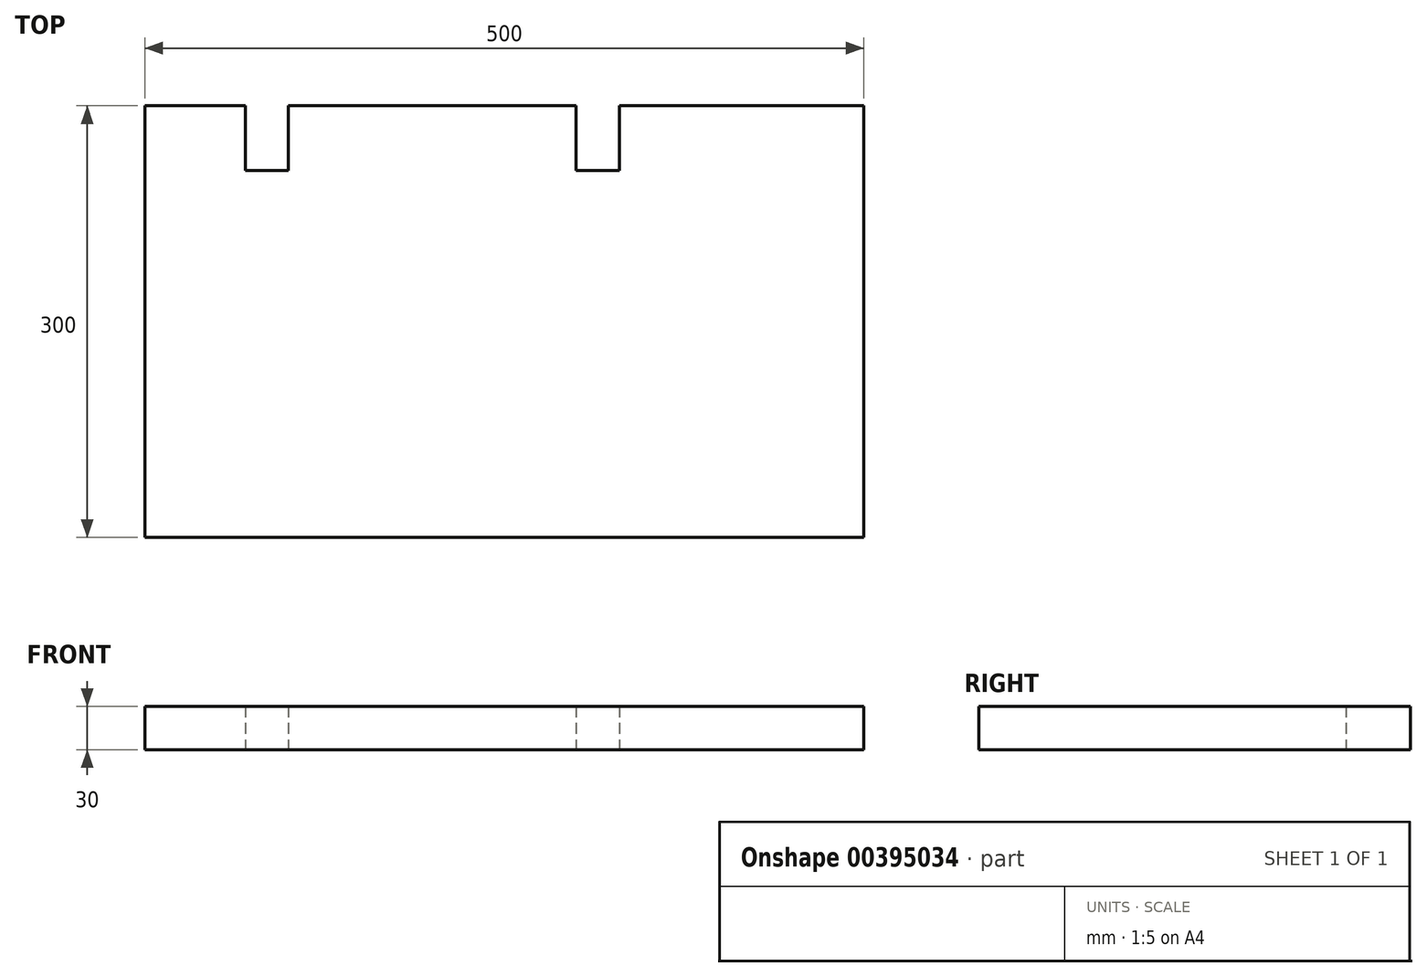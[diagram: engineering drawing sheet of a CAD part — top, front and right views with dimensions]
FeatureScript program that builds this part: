
annotation { "Feature Type Name" : "Feature", "Feature Type Description" : "" }
export const myFeature = defineFeature(function(context is Context, id is Id, definition is map)
    precondition{}
    {
        {
            var Q0;
            Q0=qCreatedBy(makeId("Front.planeOp"),FACE);
            var sketch = newSketch(context, id + "F0", { "sketchPlane" : qUnion([Q0])});
            skLineSegment(sketch, "E0.bottom", {"start": v(-250, 15) * mm, "end": v(250, 15) * mm});
            skLineSegment(sketch, "E0.top", {"start": v(-250, -15) * mm, "end": v(250, -15) * mm});
            skLineSegment(sketch, "E0.left", {"start": v(-250, 15) * mm, "end": v(-250, -15) * mm});
            skLineSegment(sketch, "E0.right", {"start": v(250, 15) * mm, "end": v(250, -15) * mm});
            skPoint(sketch, "E0.middle", {"position": v(0, 0) * mm});
            skSolve(sketch);
        }
        {
            var Q0;
            Q0=makeQuery(id+"F0.imprint","IMPRINT",FACE,{"disambiguationData":[TD([[makeQuery(id+"F0.imprint","IMPRINT",EDGE,{"derivedFrom":sQuery(id+"F0.wireOp",EDGE,"E0.bottom")}),-1.0]])]});
            extrude(context, id + "F1", {"entities" : qUnion([Q0]), "depth" : 300 * mm});
        }
        {
            var Q0;
            Q0=qCreatedBy(makeId("Front.planeOp"),FACE);
            var sketch = newSketch(context, id + "F2", { "sketchPlane" : qUnion([Q0])});
            skLineSegment(sketch, "E1.bottom", {"start": v(80, 15) * mm, "end": v(50, 15) * mm});
            skLineSegment(sketch, "E1.top", {"start": v(80, -15) * mm, "end": v(50, -15) * mm});
            skLineSegment(sketch, "E1.left", {"start": v(50, 15) * mm, "end": v(50, -15) * mm});
            skLineSegment(sketch, "E1.right", {"start": v(80, 15) * mm, "end": v(80, -15) * mm});
            skSolve(sketch);
        }
        {
            var Q0;
            Q0=qSketchRegion(id+"F2",true);
            extrude(context, id + "F3", {"entities" : qUnion([Q0]), "operationType" : NewBodyOperationType.REMOVE, "depth" : 45 * mm});
        }
        {
            var Q0;
            Q0=qCreatedBy(makeId("Front.planeOp"),FACE);
            var sketch = newSketch(context, id + "F4", { "sketchPlane" : qUnion([Q0])});
            skLineSegment(sketch, "E2.bottom", {"start": v(-150, 15) * mm, "end": v(-180, 15) * mm});
            skLineSegment(sketch, "E2.top", {"start": v(-150, -15) * mm, "end": v(-180, -15) * mm});
            skLineSegment(sketch, "E2.left", {"start": v(-150, 15) * mm, "end": v(-150, -15) * mm});
            skLineSegment(sketch, "E2.right", {"start": v(-180, 15) * mm, "end": v(-180, -15) * mm});
            skSolve(sketch);
        }
        {
            var Q0;
            Q0=qSketchRegion(id+"F4",true);
            extrude(context, id + "F5", {"entities" : qUnion([Q0]), "operationType" : NewBodyOperationType.REMOVE, "depth" : 45 * mm});
        }
    });
